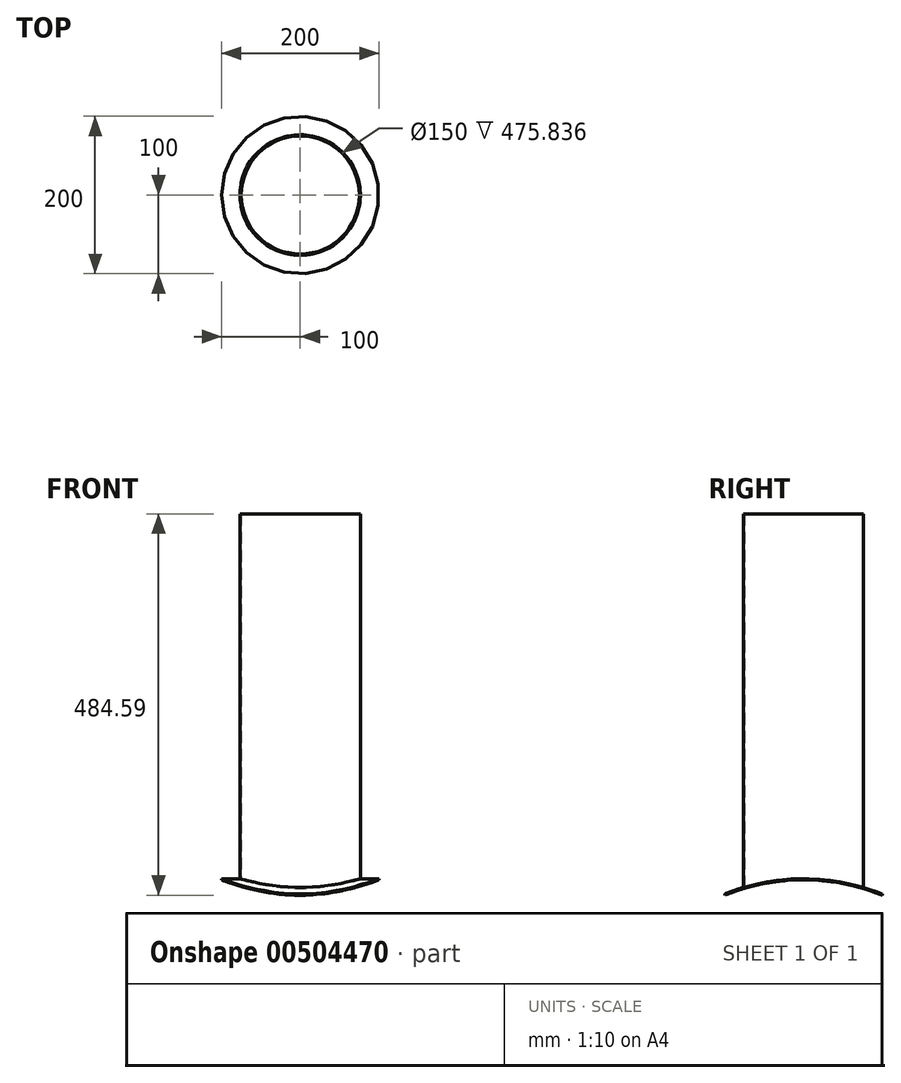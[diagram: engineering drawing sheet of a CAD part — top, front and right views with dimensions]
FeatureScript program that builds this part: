
annotation { "Feature Type Name" : "Feature", "Feature Type Description" : "" }
export const myFeature = defineFeature(function(context is Context, id is Id, definition is map)
    precondition{}
    {
        {
            var Q0;
            Q0=qCreatedBy(makeId("Right.planeOp"),FACE);
            var sketch = newSketch(context, id + "F0", { "sketchPlane" : qUnion([Q0])});
            skArc(sketch, "E0", {"start": v(131.62, 0) * mm, "mid": v(0, 35) * mm, "end": v(-131.62, 0) * mm});
            skArc(sketch, "E1", {"start": v(134.62, 0) * mm, "mid": v(0, 36.5) * mm, "end": v(-134.62, 0) * mm});
            skLineSegment(sketch, "E2", {"start": v(134.62, 0) * mm, "end": v(131.62, 0) * mm});
            skLineSegment(sketch, "E3", {"start": v(-131.62, 0) * mm, "end": v(-134.62, 0) * mm});
            skSolve(sketch);
        }
        {
            var Q0;
            Q0=makeQuery(id+"F0.imprint","IMPRINT",FACE,{"disambiguationData":[TD([[makeQuery(id+"F0.imprint","IMPRINT",EDGE,{"derivedFrom":sQuery(id+"F0.wireOp",EDGE,"E0")}),-1.0]])]});
            extrude(context, id + "F1", {"entities" : qUnion([Q0]), "depth" : 125 * mm, "hasSecondDirection" : true, "secondDirectionOppositeDirection" : true, "secondDirectionDepth" : 125 * mm});
        }
        {
            var Q0;
            Q0=qCreatedBy(makeId("Top.planeOp"),FACE);
            var sketch = newSketch(context, id + "F2", { "sketchPlane" : qUnion([Q0])});
            skCircle(sketch, "E4", {"center": v(0, 0) * mm, "radius": 75 * mm});
            skCircle(sketch, "E5", {"center": v(0, 0) * mm, "radius": 100 * mm});
            skCircle(sketch, "E6", {"center": v(0, 0) * mm, "radius": 250 * mm});
            skSolve(sketch);
        }
        {
            var Q0;
            Q0=makeQuery(id+"F2.imprint","IMPRINT",FACE,{"disambiguationData":[TD([[makeQuery(id+"F2.imprint","IMPRINT",EDGE,{"derivedFrom":sQuery(id+"F2.wireOp",EDGE,"E4")}),1.0]])]});
            var Q1;
            Q1=makeQuery(id+"F2.imprint","IMPRINT",FACE,{"disambiguationData":[TD([[makeQuery(id+"F2.imprint","IMPRINT",EDGE,{"derivedFrom":sQuery(id+"F2.wireOp",EDGE,"E5")}),-1.0]])]});
            extrude(context, id + "F3", {"entities" : qUnion([Q0, Q1]), "operationType" : NewBodyOperationType.REMOVE, "endBound" : BoundingType.THROUGH_ALL, "depth" : 25 * mm});
        }
        {
            var Q0;
            Q0=qCreatedBy(makeId("Top.planeOp"),FACE);
            cPlane(context, id + "F4", {"entities" : qUnion([Q0]), "cplaneType" : CPlaneType.OFFSET, "offset" : 500 * mm, "width" : 150 * mm, "height" : 150 * mm});
        }
        {
            var Q0;
            Q0=qCreatedBy(id+"F4.planeOp",FACE);
            var sketch = newSketch(context, id + "F5", { "sketchPlane" : qUnion([Q0])});
            skCircle(sketch, "E7.0", {"center": v(0, 0) * mm, "radius": 75 * mm});
            skCircle(sketch, "E8", {"center": v(0, 0) * mm, "radius": 76.5 * mm});
            skSolve(sketch);
        }
        {
            var Q0;
            Q0=makeQuery(id+"F5.imprint","IMPRINT",FACE,{"disambiguationData":[TD([[makeQuery(id+"F5.imprint","IMPRINT",EDGE,{"derivedFrom":sQuery(id+"F5.wireOp",EDGE,"E7.0")}),-1.0]])]});
            var Q1;
            Q1=makeQuery(id+"F1.opExtrude","SWEPT_FACE",FACE,{"disambiguationData":[OSD([sQuery(id+"F0.wireOp",EDGE,"E1")])]});
            extrude(context, id + "F6", {"entities" : qUnion([Q0]), "operationType" : NewBodyOperationType.ADD, "endBound" : BoundingType.UP_TO_SURFACE, "oppositeDirection" : true, "endBoundEntityFace" : qUnion([Q1]), "depth" : 25 * mm});
        }
    });
